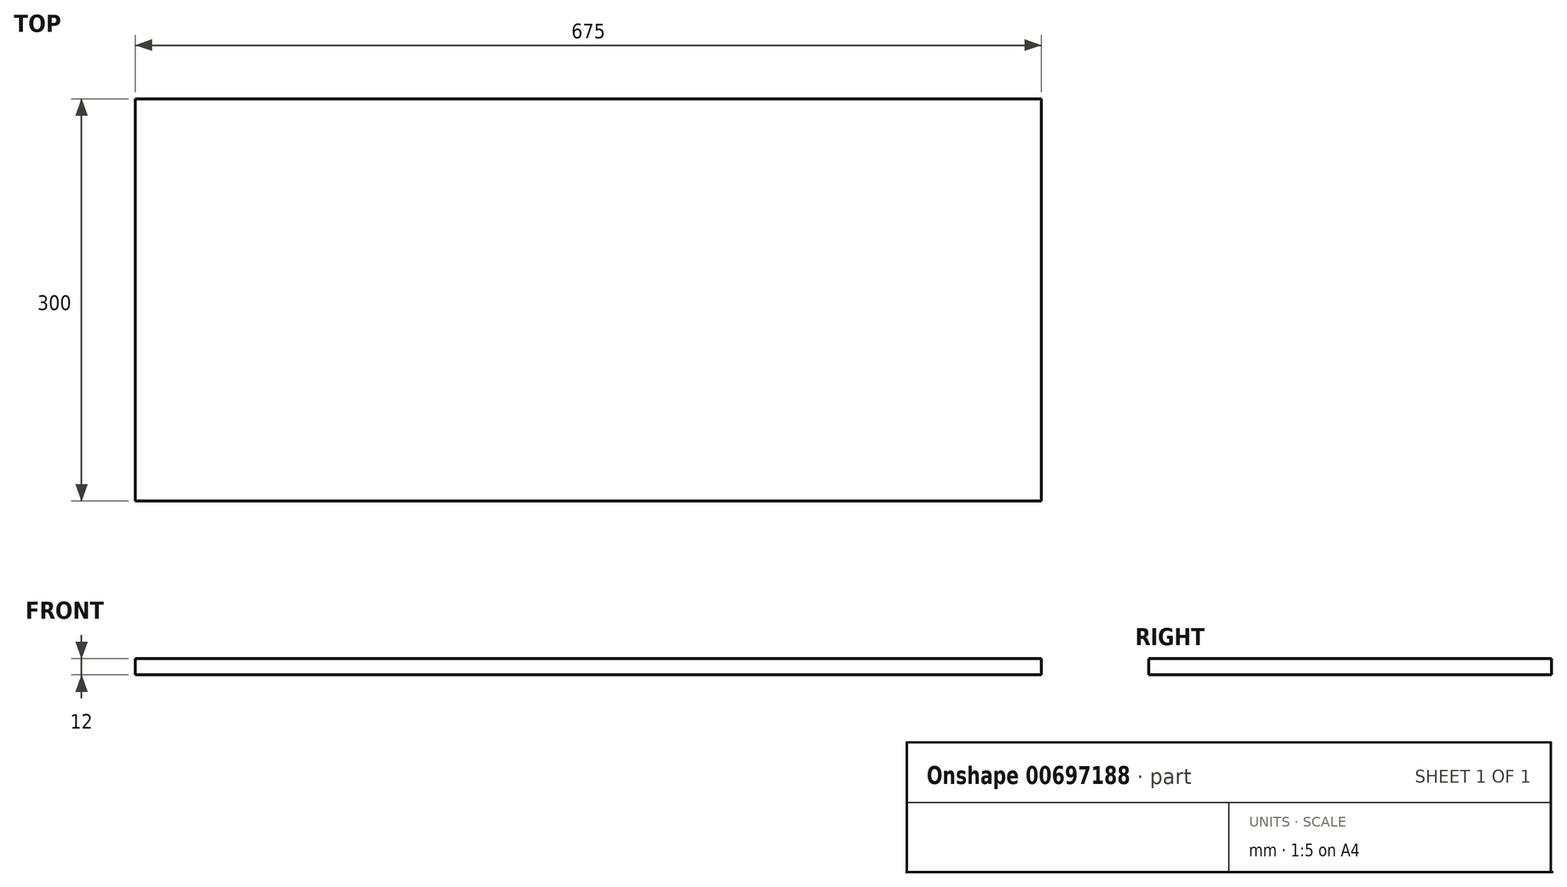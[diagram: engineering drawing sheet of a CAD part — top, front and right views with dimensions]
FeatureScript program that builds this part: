
annotation { "Feature Type Name" : "Feature", "Feature Type Description" : "" }
export const myFeature = defineFeature(function(context is Context, id is Id, definition is map)
    precondition{}
    {
        {
            var Q0;
            Q0=qCreatedBy(makeId("Top.planeOp"),FACE);
            var sketch = newSketch(context, id + "F0", { "sketchPlane" : qUnion([Q0])});
            skLineSegment(sketch, "E0.bottom", {"start": v(337.5, -150) * mm, "end": v(-337.5, -150) * mm});
            skLineSegment(sketch, "E0.top", {"start": v(337.5, 150) * mm, "end": v(-337.5, 150) * mm});
            skLineSegment(sketch, "E0.left", {"start": v(337.5, -150) * mm, "end": v(337.5, 150) * mm});
            skLineSegment(sketch, "E0.right", {"start": v(-337.5, -150) * mm, "end": v(-337.5, 150) * mm});
            skPoint(sketch, "E0.middle", {"position": v(0, 0) * mm});
            skSolve(sketch);
        }
        {
            var Q0;
            Q0=qSketchRegion(id+"F0",true);
            extrude(context, id + "F1", {"entities" : qUnion([Q0]), "depth" : 12 * mm, "offsetDistance" : 25 * mm});
        }
    });
